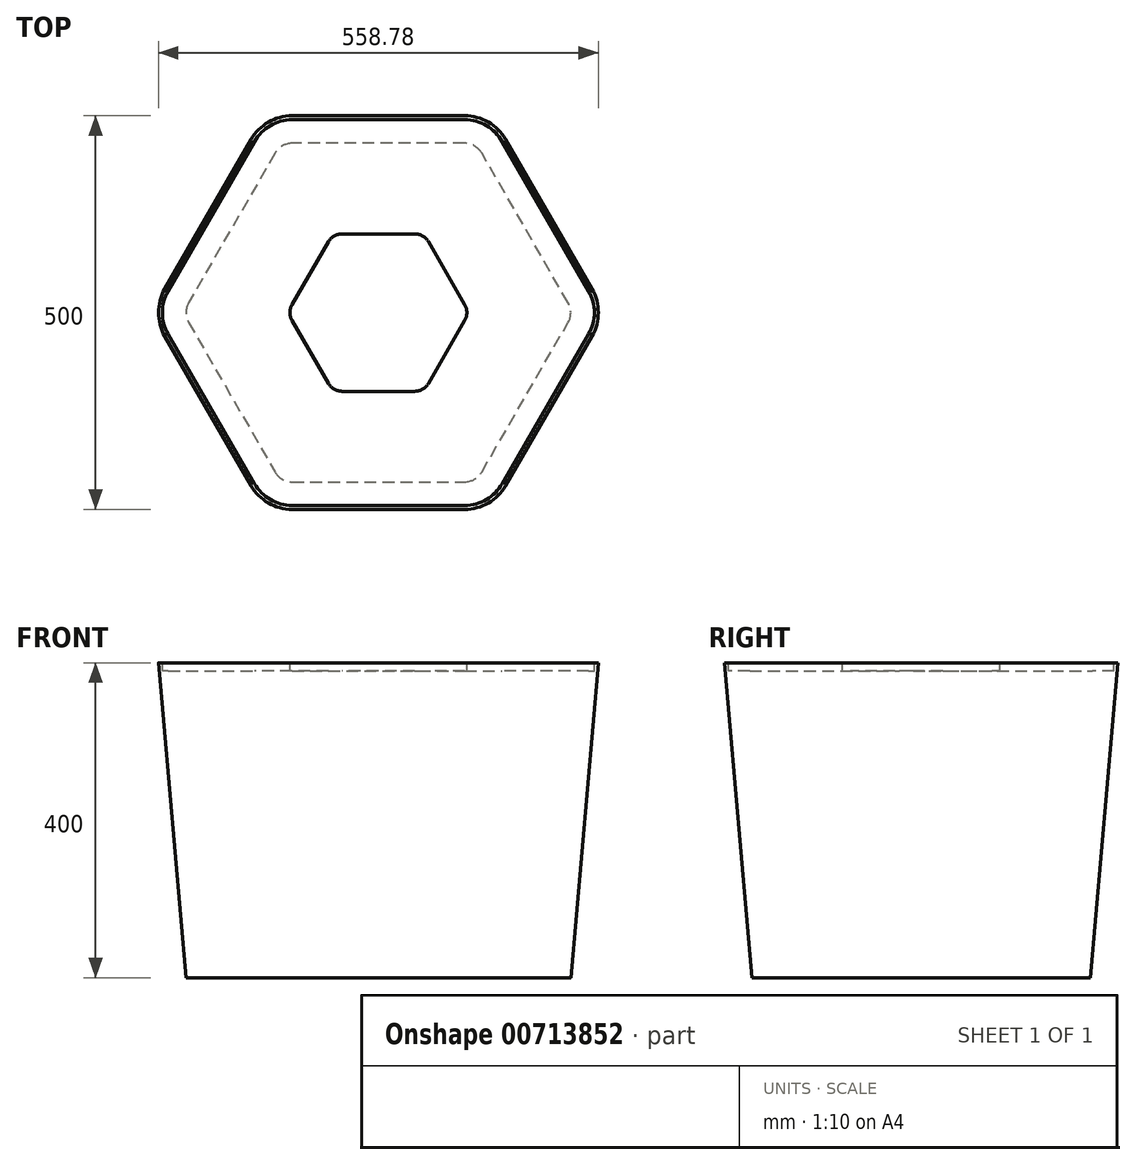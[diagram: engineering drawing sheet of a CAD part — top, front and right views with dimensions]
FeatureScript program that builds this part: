
annotation { "Feature Type Name" : "Feature", "Feature Type Description" : "" }
export const myFeature = defineFeature(function(context is Context, id is Id, definition is map)
    precondition{}
    {
        {
            var Q0;
            Q0=qCreatedBy(makeId("Top.planeOp"),FACE);
            var sketch = newSketch(context, id + "F0", { "sketchPlane" : qUnion([Q0])});
            skCircle(sketch, "E0.cCircle", {"center": v(0, 0) * mm, "radius": 250 * mm, "construction": true});
            skLineSegment(sketch, "E0.0", {"start": v(-109.7, 250) * mm, "end": v(109.7, 250) * mm});
            skLineSegment(sketch, "E0.1", {"start": v(161.66, 220) * mm, "end": v(271.35, 30) * mm});
            skLineSegment(sketch, "E0.2", {"start": v(271.35, -30) * mm, "end": v(161.66, -220) * mm});
            skLineSegment(sketch, "E0.3", {"start": v(109.7, -250) * mm, "end": v(-109.7, -250) * mm});
            skLineSegment(sketch, "E0.4", {"start": v(-161.66, -220) * mm, "end": v(-271.35, -30) * mm});
            skLineSegment(sketch, "E0.5", {"start": v(-271.35, 30) * mm, "end": v(-161.66, 220) * mm});
            skPoint(sketch, "E0.0.midPoint", {"position": v(0, 250) * mm});
            skPoint(sketch, "E1.visualSharp", {"position": v(-144.34, 250) * mm});
            skArc(sketch, "E1.filletArc", {"start": v(-109.7, 250) * mm, "mid": v(-139.7, 241.96) * mm, "end": v(-161.66, 220) * mm});
            skPoint(sketch, "E2.visualSharp", {"position": v(144.34, 250) * mm});
            skArc(sketch, "E2.filletArc", {"start": v(161.66, 220) * mm, "mid": v(139.7, 241.96) * mm, "end": v(109.7, 250) * mm});
            skPoint(sketch, "E3.visualSharp", {"position": v(288.68, 0) * mm});
            skArc(sketch, "E3.filletArc", {"start": v(271.35, -30) * mm, "mid": v(279.4, 0) * mm, "end": v(271.35, 30) * mm});
            skPoint(sketch, "E4.visualSharp", {"position": v(144.34, -250) * mm});
            skArc(sketch, "E4.filletArc", {"start": v(109.7, -250) * mm, "mid": v(139.7, -241.96) * mm, "end": v(161.66, -220) * mm});
            skPoint(sketch, "E5.visualSharp", {"position": v(-144.34, -250) * mm});
            skArc(sketch, "E5.filletArc", {"start": v(-161.66, -220) * mm, "mid": v(-139.7, -241.96) * mm, "end": v(-109.7, -250) * mm});
            skPoint(sketch, "E6.visualSharp", {"position": v(-288.68, 0) * mm});
            skArc(sketch, "E6.filletArc", {"start": v(-271.35, 30) * mm, "mid": v(-279.4, 0) * mm, "end": v(-271.35, -30) * mm});
            skArc(sketch, "E7.0", {"start": v(-157.33, -217.5) * mm, "mid": v(-137.2, -237.63) * mm, "end": v(-109.7, -245) * mm});
            skLineSegment(sketch, "E7.1", {"start": v(-109.7, 245) * mm, "end": v(109.7, 245) * mm});
            skArc(sketch, "E7.2", {"start": v(-109.7, 245) * mm, "mid": v(-137.2, 237.63) * mm, "end": v(-157.33, 217.5) * mm});
            skLineSegment(sketch, "E7.3", {"start": v(-267.02, 27.5) * mm, "end": v(-157.33, 217.5) * mm});
            skArc(sketch, "E7.4", {"start": v(-267.02, 27.5) * mm, "mid": v(-274.4, 0) * mm, "end": v(-267.02, -27.5) * mm});
            skArc(sketch, "E7.5", {"start": v(157.33, 217.5) * mm, "mid": v(137.2, 237.63) * mm, "end": v(109.7, 245) * mm});
            skLineSegment(sketch, "E7.6", {"start": v(-157.33, -217.5) * mm, "end": v(-267.02, -27.5) * mm});
            skLineSegment(sketch, "E7.7", {"start": v(157.33, 217.5) * mm, "end": v(267.02, 27.5) * mm});
            skArc(sketch, "E7.8", {"start": v(267.02, -27.5) * mm, "mid": v(274.4, 0) * mm, "end": v(267.02, 27.5) * mm});
            skLineSegment(sketch, "E7.9", {"start": v(267.02, -27.5) * mm, "end": v(157.33, -217.5) * mm});
            skArc(sketch, "E7.10", {"start": v(109.7, -245) * mm, "mid": v(137.2, -237.63) * mm, "end": v(157.33, -217.5) * mm});
            skLineSegment(sketch, "E7.11", {"start": v(109.7, -245) * mm, "end": v(-109.7, -245) * mm});
            skCircle(sketch, "E8.cCircle", {"center": v(0, 0) * mm, "radius": 100 * mm, "construction": true});
            skLineSegment(sketch, "E8.0", {"start": v(-46.19, 100) * mm, "end": v(46.19, 100) * mm});
            skLineSegment(sketch, "E8.1", {"start": v(63.5, 90) * mm, "end": v(109.7, 10) * mm});
            skLineSegment(sketch, "E8.2", {"start": v(109.7, -10) * mm, "end": v(63.5, -90) * mm});
            skLineSegment(sketch, "E8.3", {"start": v(46.19, -100) * mm, "end": v(-46.19, -100) * mm});
            skLineSegment(sketch, "E8.4", {"start": v(-63.5, -90) * mm, "end": v(-109.7, -10) * mm});
            skLineSegment(sketch, "E8.5", {"start": v(-109.7, 10) * mm, "end": v(-63.5, 90) * mm});
            skPoint(sketch, "E8.0.midPoint", {"position": v(0, 100) * mm});
            skPoint(sketch, "E9.visualSharp", {"position": v(-57.74, 100) * mm});
            skArc(sketch, "E9.filletArc", {"start": v(-46.19, 100) * mm, "mid": v(-56.19, 97.32) * mm, "end": v(-63.5, 90) * mm});
            skPoint(sketch, "E10.visualSharp", {"position": v(57.74, 100) * mm});
            skArc(sketch, "E10.filletArc", {"start": v(63.5, 90) * mm, "mid": v(56.19, 97.32) * mm, "end": v(46.19, 100) * mm});
            skPoint(sketch, "E11.visualSharp", {"position": v(115.47, 0) * mm});
            skArc(sketch, "E11.filletArc", {"start": v(109.7, -10) * mm, "mid": v(112.38, 0) * mm, "end": v(109.7, 10) * mm});
            skPoint(sketch, "E12.visualSharp", {"position": v(57.74, -100) * mm});
            skArc(sketch, "E12.filletArc", {"start": v(46.19, -100) * mm, "mid": v(56.19, -97.32) * mm, "end": v(63.5, -90) * mm});
            skPoint(sketch, "E13.visualSharp", {"position": v(-57.74, -100) * mm});
            skArc(sketch, "E13.filletArc", {"start": v(-63.5, -90) * mm, "mid": v(-56.19, -97.32) * mm, "end": v(-46.19, -100) * mm});
            skPoint(sketch, "E14.visualSharp", {"position": v(-115.47, 0) * mm});
            skArc(sketch, "E14.filletArc", {"start": v(-109.7, 10) * mm, "mid": v(-112.38, 0) * mm, "end": v(-109.7, -10) * mm});
            skSolve(sketch);
        }
        {
            var Q0;
            Q0 = qSketchRegion(id + "F0", true);
            var Q1;
            Q1=makeQuery(id+"F0.imprint","IMPRINT",FACE,{"disambiguationData":[TD([[makeQuery(id+"F0.imprint","IMPRINT",EDGE,{"derivedFrom":sQuery(id+"F0.wireOp",EDGE,"E7.0")}),1.0]])]});
            var Q2;
            Q2=makeQuery(id+"F0.imprint","IMPRINT",FACE,{"disambiguationData":[TD([[makeQuery(id+"F0.imprint","IMPRINT",EDGE,{"derivedFrom":sQuery(id+"F0.wireOp",EDGE,"E8.0")}),-1.0]])]});
            extrude(context, id + "F1", {"entities" : qUnion([Q0, Q1, Q2]), "oppositeDirection" : true, "depth" : 400 * mm, "offsetDistance" : 25 * mm, "hasDraft" : true, "draftAngle" : 5 * degree, "draftPullDirection" : true});
        }
        {
            var Q0;
            Q0=makeQuery(id+"F0.imprint","IMPRINT",FACE,{"disambiguationData":[TD([[makeQuery(id+"F0.imprint","IMPRINT",EDGE,{"derivedFrom":sQuery(id+"F0.wireOp",EDGE,"E7.0")}),1.0]])]});
            extrude(context, id + "F2", {"entities" : qUnion([Q0]), "operationType" : NewBodyOperationType.REMOVE, "oppositeDirection" : true, "depth" : 10 * mm, "offsetDistance" : 25 * mm});
        }
        {
            var Q0;
            Q0=qCreatedBy(makeId("Top.planeOp"),FACE);
            cPlane(context, id + "F3", {"entities" : qUnion([Q0]), "cplaneType" : CPlaneType.OFFSET, "offset" : 10 * mm, "oppositeDirection" : true, "width" : 150 * mm, "height" : 150 * mm});
        }
    });
